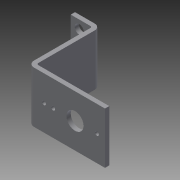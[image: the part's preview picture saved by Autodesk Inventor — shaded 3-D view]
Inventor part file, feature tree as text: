
AUTODESK INVENTOR PART (.ipt)
format: ipt  version: 2013 (Build 170138000, 138)  size: 214,016 bytes
history: native  units: in
note: dims shown in document units (in); Inventor stores cm internally (conversion verified against a paired STEP export)
features: sheet_metal_op x7, other x6, sketch x5, reference x4
ambient origin geometry x8: Origin, YZ Plane, XZ Plane, XY Plane, X Axis, Y Axis, Z Axis, Center Point
bodies: Solid1 (feature_tree)
feature tree (22):
  sheet_metal_op  "Face1"
  sheet_metal_op  "Flange1"
  sheet_metal_op  "Flange2"
  sketch  "Sketch1"  dims[d0=1.5in]
  other  "Plate1"
  sketch  "Sketch2"  dims[d1=0.75in]
  other  "Plate2"
  sheet_metal_op  "Bend1"
  sheet_metal_op  "Corner1"
  sketch  "Sketch3"  dims[d2=0.266in]
  other  "Plate3"
  sheet_metal_op  "Bend2"
  sheet_metal_op  "Corner2"
  sketch  "Sketch4"  dims[d3=0.266in]
  reference  "Reference1"
  sketch  "Sketch5"  dims[d4=1.0in d5=0.25in d6=0.25in d7=0.25in d8=0.125in d9=0.125in d10=0.0625in d11=0.25in d12=0.125in d13=2.0in d14=90.0deg d15=0.05in d16=0.5in d17=0.125in d18=0.125in d19=0.125in d20=0.0625in d21=0.25in d22=0.125in d23=2.25in d24=90.0deg d25=0.05in d26=0.5in d27=0.125in d28=0.125in d29=0.5in d31=0.125in d32=0.0in d33=0.125in d34=0.0in]
  reference  "Reference2"
  reference  "Reference3"
  reference  "Reference4"
  other  "Cut1"
  other  "Cut2"
  other  "Definition1"
